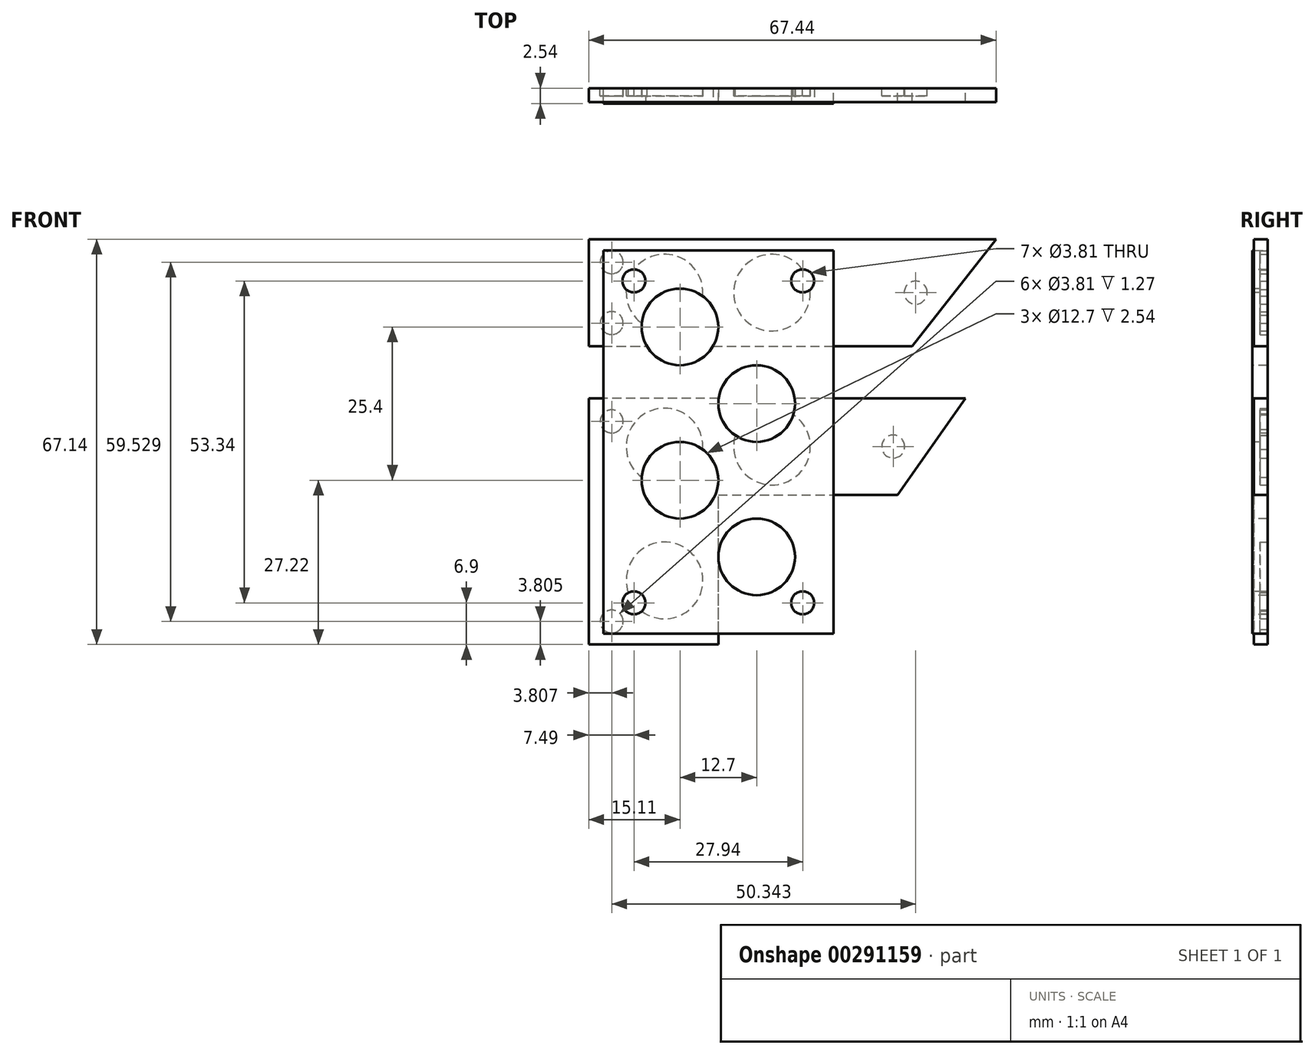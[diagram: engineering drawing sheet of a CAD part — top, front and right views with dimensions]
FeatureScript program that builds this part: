
annotation { "Feature Type Name" : "Feature", "Feature Type Description" : "" }
export const myFeature = defineFeature(function(context is Context, id is Id, definition is map)
    precondition{}
    {
        {
            var Q0;
            Q0=qCreatedBy(makeId("Front.planeOp"),FACE);
            var sketch = newSketch(context, id + "F0", { "sketchPlane" : qUnion([Q0])});
            skLineSegment(sketch, "E0", {"start": v(-21.46, 7.2) * mm, "end": v(-21.46, -33.57) * mm});
            skLineSegment(sketch, "E1", {"start": v(-21.46, -33.57) * mm, "end": v(0, -33.57) * mm});
            skLineSegment(sketch, "E2", {"start": v(0, -33.57) * mm, "end": v(0, -8.76) * mm});
            skLineSegment(sketch, "E3", {"start": v(0, -8.76) * mm, "end": v(29.67, -8.76) * mm});
            skLineSegment(sketch, "E4", {"start": v(29.67, -8.76) * mm, "end": v(40.95, 7.2) * mm});
            skLineSegment(sketch, "E5", {"start": v(40.95, 7.2) * mm, "end": v(-21.46, 7.2) * mm});
            skLineSegment(sketch, "E6", {"start": v(32.1, 15.88) * mm, "end": v(45.98, 33.57) * mm});
            skLineSegment(sketch, "E7", {"start": v(45.98, 33.57) * mm, "end": v(-21.46, 33.57) * mm});
            skLineSegment(sketch, "E8", {"start": v(-21.46, 33.57) * mm, "end": v(-21.46, 15.88) * mm});
            skLineSegment(sketch, "E9", {"start": v(-21.46, 15.88) * mm, "end": v(32.1, 15.88) * mm});
            skCircle(sketch, "E10", {"center": v(8.9, -0.78) * mm, "radius": 6.35 * mm, "construction": true});
            skLineSegment(sketch, "E11", {"start": v(0, -33.57) * mm, "end": v(0, 33.57) * mm, "construction": true});
            skLineSegment(sketch, "E12", {"start": v(35.3, -0.78) * mm, "end": v(-21.46, -0.78) * mm, "construction": true});
            skCircle(sketch, "E13", {"center": v(-8.89, -22.96) * mm, "radius": 6.35 * mm, "construction": true});
            skCircle(sketch, "E14", {"center": v(-8.9, 24.73) * mm, "radius": 6.35 * mm, "construction": true});
            skCircle(sketch, "E15", {"center": v(8.9, 24.73) * mm, "radius": 6.35 * mm, "construction": true});
            skCircle(sketch, "E16", {"center": v(-8.9, -0.78) * mm, "radius": 6.35 * mm, "construction": true});
            skLineSegment(sketch, "E17", {"start": v(39.04, 24.73) * mm, "end": v(-21.46, 24.73) * mm, "construction": true});
            skSolve(sketch);
        }
        {
            var Q0;
            Q0 = qSketchRegion(id + "F0", true);
            extrude(context, id + "F1", {"entities" : qUnion([Q0]), "depth" : 7.37 * mm});
        }
        {
            var Q0;
            Q0=makeQuery(id+"F0.imprint","IMPRINT",FACE,{"disambiguationData":[TD([[makeQuery(id+"F0.imprint","IMPRINT",EDGE,{"derivedFrom":sQuery(id+"F0.wireOp",EDGE,"E6")}),1.0]])]});
            var sketch = newSketch(context, id + "F2", { "sketchPlane" : qUnion([Q0])});
            skCircle(sketch, "E18", {"center": v(-8.9, 24.73) * mm, "radius": 6.35 * mm});
            skCircle(sketch, "E19", {"center": v(8.9, 24.73) * mm, "radius": 6.35 * mm});
            skCircle(sketch, "E20", {"center": v(8.9, -0.78) * mm, "radius": 6.35 * mm});
            skCircle(sketch, "E21", {"center": v(-8.9, -0.78) * mm, "radius": 6.35 * mm});
            skCircle(sketch, "E22", {"center": v(-8.89, -22.96) * mm, "radius": 6.35 * mm});
            skCircle(sketch, "E23", {"center": v(32.7, 24.73) * mm, "radius": 1.9 * mm});
            skCircle(sketch, "E24", {"center": v(-17.65, 29.76) * mm, "radius": 1.9 * mm});
            skCircle(sketch, "E25", {"center": v(-17.65, 19.69) * mm, "radius": 1.9 * mm});
            skCircle(sketch, "E26", {"center": v(28.96, -0.78) * mm, "radius": 1.9 * mm});
            skCircle(sketch, "E27", {"center": v(-17.65, 3.4) * mm, "radius": 1.9 * mm});
            skCircle(sketch, "E28", {"center": v(-17.65, -29.76) * mm, "radius": 1.9 * mm});
            skSolve(sketch);
        }
        {
            var Q0;
            Q0=qCreatedBy(makeId("Front.planeOp"),FACE);
            var sketch = newSketch(context, id + "F3", { "sketchPlane" : qUnion([Q0])});
            skLineSegment(sketch, "E29.bottom", {"start": v(19.05, -31.75) * mm, "end": v(-19.05, -31.75) * mm});
            skLineSegment(sketch, "E29.top", {"start": v(19.05, 31.75) * mm, "end": v(-19.05, 31.75) * mm});
            skLineSegment(sketch, "E29.left", {"start": v(19.05, -31.75) * mm, "end": v(19.05, 31.75) * mm});
            skLineSegment(sketch, "E29.right", {"start": v(-19.05, -31.75) * mm, "end": v(-19.05, 31.75) * mm});
            skPoint(sketch, "E29.middle", {"position": v(0, 0) * mm});
            skSolve(sketch);
        }
        {
            var Q0;
            Q0 = qSketchRegion(id + "F3", true);
            extrude(context, id + "F4", {"entities" : qUnion([Q0]), "depth" : 7.62 * mm});
        }
        {
            var Q0;
            Q0=makeQuery(id+"F4.opExtrude","CAP_FACE",FACE,{"disambiguationData":[OSD([sQuery(id+"F3.wireOp",EDGE,"E29.bottom"),sQuery(id+"F3.wireOp",EDGE,"E29.top"),sQuery(id+"F3.wireOp",EDGE,"E29.left"),sQuery(id+"F3.wireOp",EDGE,"E29.right")])],"isStart":false});
            var sketch = newSketch(context, id + "F5", { "sketchPlane" : qUnion([Q0])});
            skCircle(sketch, "E30", {"center": v(-6.35, 19.05) * mm, "radius": 6.35 * mm});
            skCircle(sketch, "E31", {"center": v(6.35, 6.35) * mm, "radius": 6.35 * mm});
            skCircle(sketch, "E32", {"center": v(-6.35, -6.35) * mm, "radius": 6.35 * mm});
            skCircle(sketch, "E33", {"center": v(6.35, -19.05) * mm, "radius": 6.35 * mm});
            skCircle(sketch, "E34", {"center": v(13.97, 26.67) * mm, "radius": 1.9 * mm});
            skCircle(sketch, "E35", {"center": v(13.97, -26.67) * mm, "radius": 1.9 * mm});
            skCircle(sketch, "E36", {"center": v(-13.97, -26.67) * mm, "radius": 1.9 * mm});
            skCircle(sketch, "E37", {"center": v(-13.97, 26.67) * mm, "radius": 1.9 * mm});
            skSolve(sketch);
        }
        {
            var Q0;
            Q0 = qSketchRegion(id + "F5", true);
            extrude(context, id + "F6", {"entities" : qUnion([Q0]), "operationType" : NewBodyOperationType.REMOVE, "oppositeDirection" : true, "depth" : 6.35 * mm});
        }
        {
            var Q0;
            Q0 = qSketchRegion(id + "F2", true);
            extrude(context, id + "F7", {"entities" : qUnion([Q0]), "operationType" : NewBodyOperationType.REMOVE, "depth" : 6.35 * mm});
        }
        {
            var Q0;
            Q0=makeQuery(id+"F0.imprint","IMPRINT",FACE,{"disambiguationData":[TD([[makeQuery(id+"F0.imprint","IMPRINT",EDGE,{"derivedFrom":sQuery(id+"F0.wireOp",EDGE,"E6")}),1.0]])]});
            var sketch = newSketch(context, id + "F8", { "sketchPlane" : qUnion([Q0])});
            skLineSegment(sketch, "E38.bottom", {"start": v(56.53, 48.42) * mm, "end": v(-56.53, 48.42) * mm});
            skLineSegment(sketch, "E38.top", {"start": v(56.53, -48.42) * mm, "end": v(-56.53, -48.42) * mm});
            skLineSegment(sketch, "E38.left", {"start": v(56.53, 48.42) * mm, "end": v(56.53, -48.42) * mm});
            skLineSegment(sketch, "E38.right", {"start": v(-56.53, 48.42) * mm, "end": v(-56.53, -48.42) * mm});
            skPoint(sketch, "E38.middle", {"position": v(0, 0) * mm});
            skSolve(sketch);
        }
        {
            var Q0;
            Q0 = qSketchRegion(id + "F8", true);
            extrude(context, id + "F9", {"entities" : qUnion([Q0]), "operationType" : NewBodyOperationType.REMOVE, "depth" : 5.08 * mm});
        }
    });
